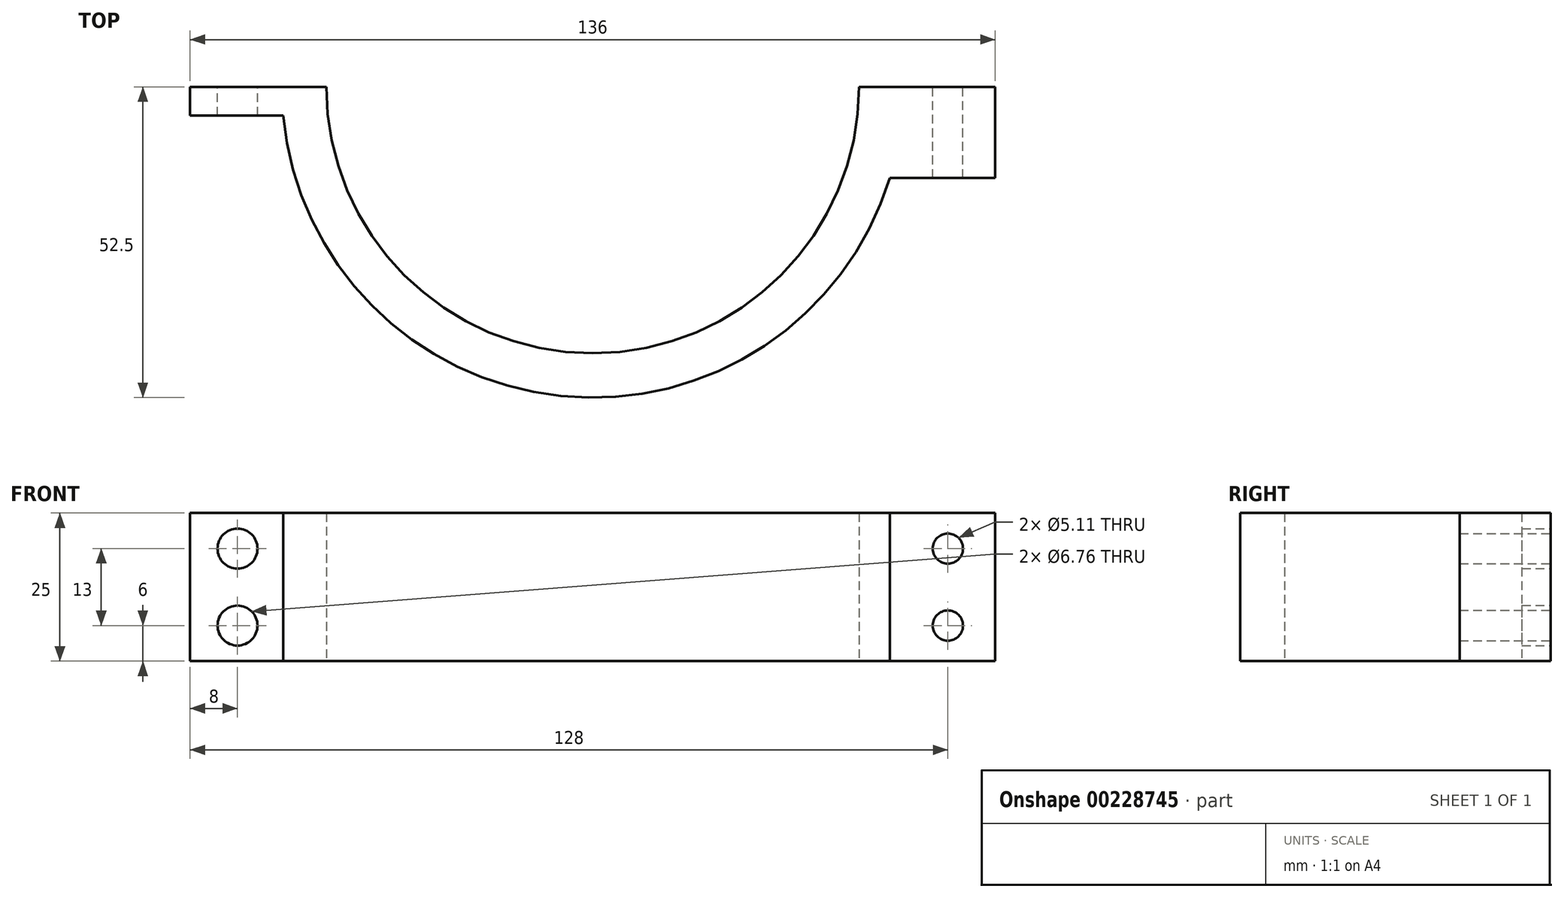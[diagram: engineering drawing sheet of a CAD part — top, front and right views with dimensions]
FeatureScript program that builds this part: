
annotation { "Feature Type Name" : "Feature", "Feature Type Description" : "" }
export const myFeature = defineFeature(function(context is Context, id is Id, definition is map)
    precondition{}
    {
        {
            var Q0;
            Q0=qCreatedBy(makeId("Top.planeOp"),FACE);
            var sketch = newSketch(context, id + "F0", { "sketchPlane" : qUnion([Q0])});
            skArc(sketch, "E0", {"start": v(-45, 0) * mm, "mid": v(0, -45) * mm, "end": v(45, 0) * mm});
            skArc(sketch, "E1", {"start": v(-52.27, -4.88) * mm, "mid": v(-5.37, -52.22) * mm, "end": v(50.19, -15.41) * mm});
            skLineSegment(sketch, "E2", {"start": v(-45, 0) * mm, "end": v(-68, 0) * mm});
            skLineSegment(sketch, "E3", {"start": v(-68, 0) * mm, "end": v(-68, -4.88) * mm});
            skLineSegment(sketch, "E4", {"start": v(-68, -4.88) * mm, "end": v(-52.27, -4.88) * mm});
            skLineSegment(sketch, "E5", {"start": v(45, 0) * mm, "end": v(68, 0) * mm});
            skLineSegment(sketch, "E6", {"start": v(68, 0) * mm, "end": v(68, -15.41) * mm});
            skPoint(sketch, "E7.orphan", {"position": v(52.5, 0) * mm});
            skLineSegment(sketch, "E8", {"start": v(0, 0) * mm, "end": v(69.96, -69.96) * mm, "construction": true});
            skLineSegment(sketch, "E9", {"start": v(68, -25.57) * mm, "end": v(79.96, -37.54) * mm});
            skPoint(sketch, "E10.orphan", {"position": v(68, -4.88) * mm});
            skLineSegment(sketch, "E11", {"start": v(68, -15.41) * mm, "end": v(50.19, -15.41) * mm});
            skSolve(sketch);
        }
        {
            var Q0;
            Q0=qSketchRegion(id+"F0",true);
            extrude(context, id + "F1", {"entities" : qUnion([Q0]), "depth" : 25 * mm});
        }
        {
            var Q0;
            Q0=makeQuery(id+"F1.opExtrude","CAP_FACE",FACE,{"disambiguationData":[OSD([sQuery(id+"F0.wireOp",EDGE,"E0"),sQuery(id+"F0.wireOp",EDGE,"E1"),sQuery(id+"F0.wireOp",EDGE,"E2"),sQuery(id+"F0.wireOp",EDGE,"E3"),sQuery(id+"F0.wireOp",EDGE,"E4"),sQuery(id+"F0.wireOp",EDGE,"E5"),sQuery(id+"F0.wireOp",EDGE,"E6"),sQuery(id+"F0.wireOp",EDGE,"vUzMyOly-JOfE-7hCi-1u2C-14JDmTcw4MLE"),sQuery(id+"F0.wireOp",EDGE,"E9"),sQuery(id+"F0.wireOp",EDGE,"rxlOmpg4-H1yA-sSM8-2vBI-2d3FxBGD5JUs"),sQuery(id+"F0.wireOp",EDGE,"IeHL9BJB-rejn-RVMh-nobd-7hv0QQswIat9"),sQuery(id+"F0.wireOp",EDGE,"646cdaaa-5258-48e4-b4b1-44ca3091abd8.trimOffspring")])],"isStart":false});
            var sketch = newSketch(context, id + "F2", { "sketchPlane" : qUnion([Q0])});
            skLineSegment(sketch, "E12", {"start": v(-68, 0) * mm, "end": v(79.96, 0) * mm, "construction": true});
            skSolve(sketch);
        }
        {
            var Q0;
            Q0=makeQuery(id+"F1.opExtrude","SWEPT_FACE",FACE,{"disambiguationData":[OSD([sQuery(id+"F0.wireOp",EDGE,"E2")])]});
            var sketch = newSketch(context, id + "F3", { "sketchPlane" : qUnion([Q0])});
            skLineSegment(sketch, "E13", {"start": v(60, -9.06) * mm, "end": v(60, 40.75) * mm, "construction": true});
            skLineSegment(sketch, "E14", {"start": v(-60, -8.44) * mm, "end": v(-60, 38.68) * mm, "construction": true});
            skPoint(sketch, "E15", {"position": v(60, 6) * mm});
            skPoint(sketch, "E16", {"position": v(60, 19) * mm});
            skPoint(sketch, "E17", {"position": v(-60, 6) * mm});
            skPoint(sketch, "E18", {"position": v(-60, 19) * mm});
            skSolve(sketch);
        }
        {
            var Q0;
            Q0=sQuery(id+"F3.wireOp",VERTEX,"E17");
            var Q1;
            Q1=sQuery(id+"F3.wireOp",VERTEX,"E18");
            var Q2;
            Q2=makeQuery(id+"F1.opExtrude","SWEPT_BODY",BODY,{"disambiguationData":[OSD([sQuery(id+"F0.wireOp",EDGE,"E0"),sQuery(id+"F0.wireOp",EDGE,"E1"),sQuery(id+"F0.wireOp",EDGE,"E2"),sQuery(id+"F0.wireOp",EDGE,"E3"),sQuery(id+"F0.wireOp",EDGE,"E4"),sQuery(id+"F0.wireOp",EDGE,"E5"),sQuery(id+"F0.wireOp",EDGE,"E6"),sQuery(id+"F0.wireOp",EDGE,"E9"),sQuery(id+"F0.wireOp",EDGE,"rxlOmpg4-H1yA-sSM8-2vBI-2d3FxBGD5JUs"),sQuery(id+"F0.wireOp",EDGE,"IeHL9BJB-rejn-RVMh-nobd-7hv0QQswIat9")])]});
            hole(context, id + "F4", {"style" : HoleStyle.SIMPLE, "endStyle" : HoleEndStyle.BLIND, "standardTappedOrClearance" : lookupTablePath({ "standard" : "ANSI", "engagement" : "75%", "pitch" : "20 tpi", "size" : "1/4", "type" : "Tapped" }), "standardBlindInLast" : lookupTablePath({ "standard" : "ANSI", "engagement" : "75%", "pitch" : "20 tpi", "size" : "1/4", "type" : "Tapped" }), "holeDiameter" : 5.1 * mm, "holeDepth" : 25 * mm, "locations" : qUnion([Q0, Q1]), "scope" : qUnion([Q2]), "majorDiameter" : 6.35 * mm});
        }
        {
            var Q0;
            Q0=sQuery(id+"F3.wireOp",VERTEX,"E15");
            var Q1;
            Q1=sQuery(id+"F3.wireOp",VERTEX,"E16");
            var Q2;
            Q2=makeQuery(id+"F1.opExtrude","SWEPT_BODY",BODY,{"disambiguationData":[OSD([sQuery(id+"F0.wireOp",EDGE,"E0"),sQuery(id+"F0.wireOp",EDGE,"E1"),sQuery(id+"F0.wireOp",EDGE,"E2"),sQuery(id+"F0.wireOp",EDGE,"E3"),sQuery(id+"F0.wireOp",EDGE,"E4"),sQuery(id+"F0.wireOp",EDGE,"E5"),sQuery(id+"F0.wireOp",EDGE,"E6"),sQuery(id+"F0.wireOp",EDGE,"E9"),sQuery(id+"F0.wireOp",EDGE,"rxlOmpg4-H1yA-sSM8-2vBI-2d3FxBGD5JUs"),sQuery(id+"F0.wireOp",EDGE,"IeHL9BJB-rejn-RVMh-nobd-7hv0QQswIat9")])]});
            hole(context, id + "F5", {"style" : HoleStyle.SIMPLE, "endStyle" : HoleEndStyle.BLIND, "standardTappedOrClearance" : lookupTablePath({ "standard" : "ANSI", "fit" : "Normal (ASME)", "size" : "1/4", "type" : "Clearance" }), "standardBlindInLast" : lookupTablePath({ "fit" : "Free", "standard" : "ANSI", "size" : "1/4", "type" : "Clearance" }), "holeDiameter" : 6.76 * mm, "holeDepth" : 25 * mm, "locations" : qUnion([Q0, Q1]), "scope" : qUnion([Q2])});
        }
    });
